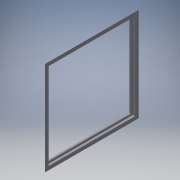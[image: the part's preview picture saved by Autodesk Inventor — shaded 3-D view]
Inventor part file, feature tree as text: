
AUTODESK INVENTOR PART (.ipt)
format: ipt  version: 2018.3 (Build 223284000, 284)  size: 157,184 bytes
history: native  units: mm
features: reference x21, extrude x4, sketch x4, projected_geometry x3, other x3, chamfer x2
ambient origin geometry x8: Origin, YZ Plane, XZ Plane, XY Plane, X Axis, Y Axis, Z Axis, Center Point
bodies: Volumenkörper1 (feature_tree)
feature tree (37):
  extrude  "Extrusion1"  Depth=440.0mm
  extrude  "Extrusion2"  Depth=17.0mm
  extrude  "Extrusion3"  Depth=17.0mm
  extrude  "Extrusion4"  Depth=10.0mm TaperAngle=0.0deg
  chamfer  "Fase1"  Distance=10.0mm
  chamfer  "Fase2"  Distance=10.0mm
  sketch  "Skizze1"  dims[d0=440.0mm d1=440.0mm]
  sketch  "Skizze2"  dims[d2=18.0mm d3=0.0mm d4=17.0mm]
  projected_geometry  "Projizierte Kontur1"
  sketch  "Skizze3"  dims[d5=17.0mm d6=17.0mm]
  projected_geometry  "Projizierte Kontur2"
  sketch  "Skizze6"  dims[d7=17.0mm d8=10.0mm d9=0.0mm d10=10.0mm d11=10.0mm d12=10.0mm d13=10.0mm d14=8.0mm d15=0.0mm d24=15.0mm d25=0.0mm d26=18.0mm d27=2.0mm d28=45.0deg d31=18.0mm d32=2.0mm d33=45.0deg]
  projected_geometry  "Projizierte Kontur4"
  reference  "Referenz29"
  reference  "Referenz30"
  reference  "Referenz31"
  reference  "Referenz32"
  reference  "Referenz33"
  reference  "Referenz34"
  reference  "Referenz35"
  reference  "Referenz36"
  reference  "Referenz37"
  reference  "Referenz38"
  reference  "Referenz39"
  reference  "Referenz40"
  reference  "Referenz41"
  reference  "Referenz42"
  reference  "Referenz43"
  reference  "Referenz44"
  reference  "Referenz45"
  reference  "Referenz46"
  reference  "Referenz47"
  reference  "Referenz48"
  reference  "Referenz49"
  parser-record x1  (decoder bookkeeping rows leaked as tree rows — omitted from the tree; the rows remain in map.json)
  other  "Baugruppe1.iam"
  other  "PV_Modul_CPY_3:1"
note: 1 file-system path scrubbed to <path> (originals preserved in map.json)
